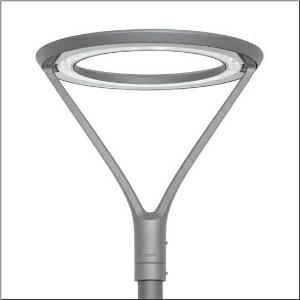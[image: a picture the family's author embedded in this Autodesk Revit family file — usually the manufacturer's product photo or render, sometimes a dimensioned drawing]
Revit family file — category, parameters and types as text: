
# Revit family: dl_20___pl1_2s_5xa51283ns008_74a5
name_source: partatom
category: Lighting Fixtures
units: mm (PartAtom-declared; Revit-internal decimal feet)

## family parameters
Cut with Voids When Loaded = No
Host = Face
Light Source = No
Part Type = Normal
Room Calculation Point = No
Round Connector Dimension = Use Diameter
Shared = No

## types (1)
- --- (1 x LED, 3060 lm, 23.2 W, 4000K)
    Apparent Load = 23 VA
    CIE Flux Codes = 33 78 99 100 100
    Color Rendering = 70
    Color Temperature = 4000K
    Default Elevation = 1800 mm
    Description = DL® 20, mast luminaire, primary light control with reflector, highly specular, primary optical cover: cover, of toughened safety glass of clear glass with excellent transmission level, light distribution: PL1.2s, light emission: direct distribution, primary light characteristic: symmetric, installation type: post-top, LED, High Power LED, rated luminous flux: 3.030lm, luminous efficacy: 111lm/W, light colour: 740, colour temperature: 4000K, control gear: Plus, control: overheat protection, power reduction, digital communication interface, constant luminous flux control, time-dependent luminous flux control, flexible luminous flux parameterisation, electronic power reduction, mains connection: 230..240V, 50/60Hz, connection cable pre-assembled, cable length: 5m, start of lifetime: 27W, end of service life: 28W, reduction: 14W, luminaire housing, upper part, of cast aluminium, powder-coated, Siteco® metallic grey (DB 702S), diameter: 690mm, height: 690mm, spigot size: 76mm (post-top), mounting height: 4..6m, luminaire housing, of cast aluminium, powder-coated, Siteco® metallic grey (DB 702S), equipment: standard, protection rating (complete): IP66, insulation class (complete): insulation class II (safety insulation), certification: CE, ENEC, VDE, impact resistance: IK08, permissible operating ambient temperature: -25..+35°C, standard-compliant lighting for roads and squares, packaging unit: 1 piece

Light Distribution: PL1.2s
    Height = 690 mm
    Lamp = 1 x LED
    Lamp Light Flux = 3060 lm
    Lamp Power = 23.2 W
    Lamp count = 1
    Length = 690 mm
    Luminous efficacy = 132 lm/W
    Manufacturer = Siteco
    ModVariant = No
    Model = 5XA51283NS008
    Number of Poles = 1
    OnlyDefault = Yes
    Power Factor = 1
    Product Name = DL 20 | PL1.2s
    Product group = mast luminaire | pylon top
    ProductGroupID = 6100
    Protection Class = Protection class II
    Protection Degree = IP 66
    RLX_Detail_Level = 1
    RLX_Emergency_Light_Flux = 0 lm
    RLX_Emergency_Type = 0
    RLX_Emergency_Type_DB = No
    RlxData = <blob elided: 204585 chars, md5=18b36186>
    Socket = socket
    Standby Power = 0 W
    System Light Flux = 3060 lm
    System Power = 23 W
    Type Comments = factory setting: luminous flux: 100 % | dim-lin: 254 | 310 mA
    Type Image = l_1006001.jpg
    URL = http://relux.com
    VarID = @adj_084375
    Voltage = 0 V
    Weight = 0.00 kg
    Width = 0 mm  [stored 0 ft]

note: [stored X ft] marks values corroborated as IEEE doubles in the binary element streams (Revit-internal decimal feet)

## geometry (parser evidence)
native form markers: Blend x4, Sweep x11
no freeform markers — native parametric forms only
